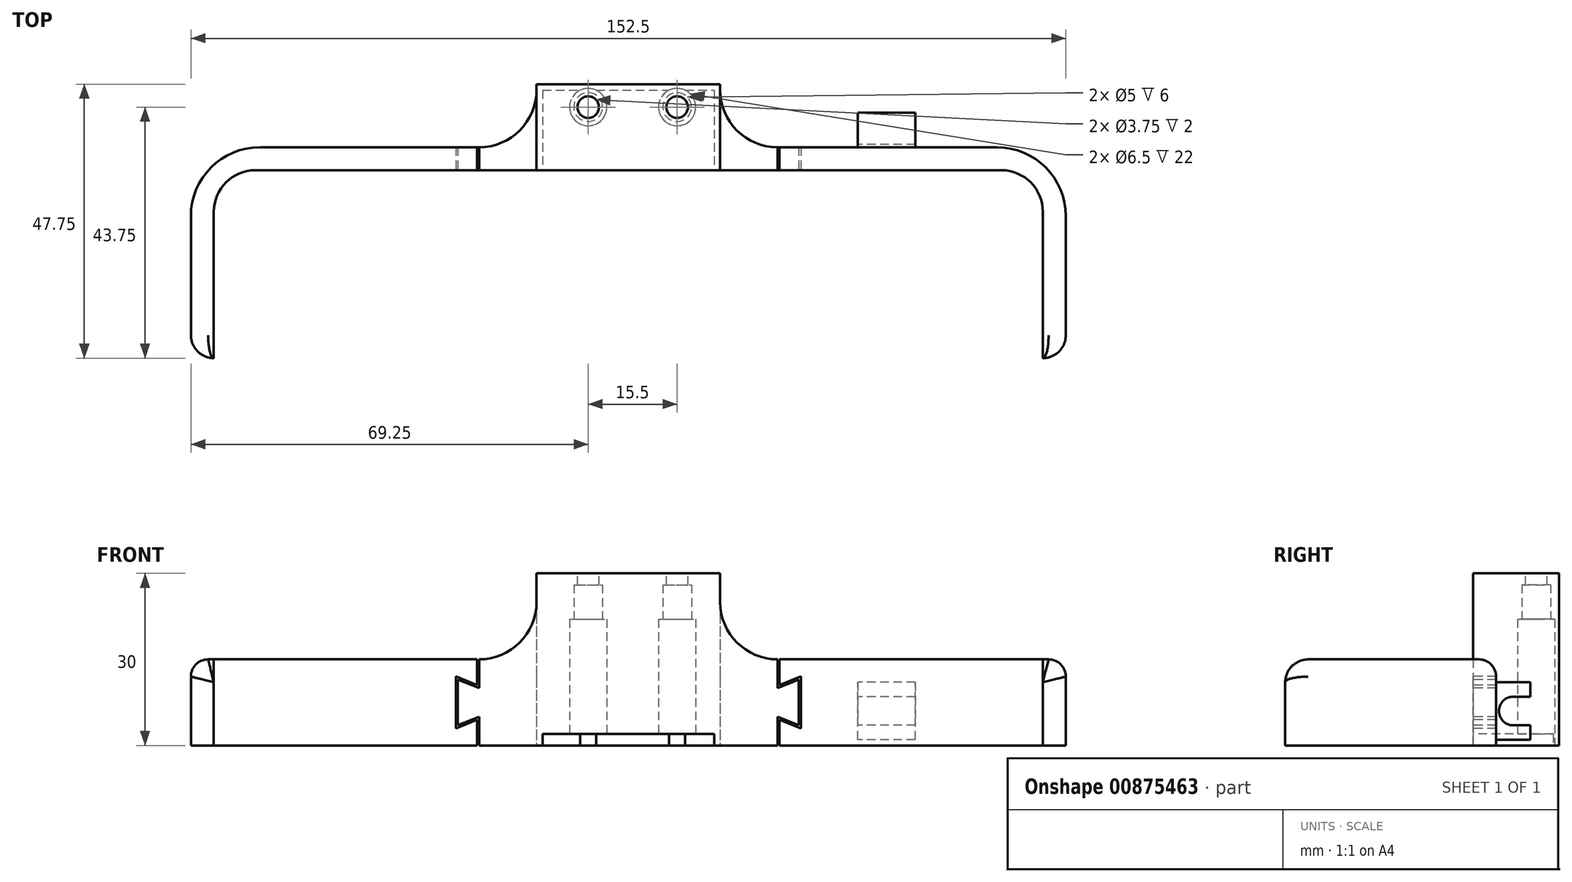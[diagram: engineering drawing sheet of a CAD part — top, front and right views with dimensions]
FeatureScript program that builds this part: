
annotation { "Feature Type Name" : "Feature", "Feature Type Description" : "" }
export const myFeature = defineFeature(function(context is Context, id is Id, definition is map)
    precondition{}
    {
        {
            var Q0;
            Q0=qCreatedBy(makeId("Top.planeOp"),FACE);
            var sketch = newSketch(context, id + "F0", { "sketchPlane" : qUnion([Q0])});
            skLineSegment(sketch, "E0.bottom", {"start": v(-65, 47.5) * mm, "end": v(65, 47.5) * mm, "construction": true});
            skLineSegment(sketch, "E0.top", {"start": v(-65, -47.5) * mm, "end": v(65, -47.5) * mm, "construction": true});
            skLineSegment(sketch, "E0.left", {"start": v(-72, 40.5) * mm, "end": v(-72, -40.5) * mm, "construction": true});
            skLineSegment(sketch, "E0.right", {"start": v(72, 40.5) * mm, "end": v(72, -40.5) * mm, "construction": true});
            skPoint(sketch, "E0.middle", {"position": v(0, 0) * mm});
            skPoint(sketch, "E1.visualSharp", {"position": v(-72, 47.5) * mm});
            skArc(sketch, "E1.filletArc", {"start": v(-65, 47.5) * mm, "mid": v(-69.95, 45.45) * mm, "end": v(-72, 40.5) * mm, "construction": true});
            skPoint(sketch, "E2.visualSharp", {"position": v(72, 47.5) * mm});
            skArc(sketch, "E2.filletArc", {"start": v(72, 40.5) * mm, "mid": v(69.95, 45.45) * mm, "end": v(65, 47.5) * mm, "construction": true});
            skPoint(sketch, "E3.visualSharp", {"position": v(72, -47.5) * mm});
            skArc(sketch, "E3.filletArc", {"start": v(65, -47.5) * mm, "mid": v(69.95, -45.45) * mm, "end": v(72, -40.5) * mm, "construction": true});
            skPoint(sketch, "E4.visualSharp", {"position": v(-72, -47.5) * mm});
            skArc(sketch, "E4.filletArc", {"start": v(-72, -40.5) * mm, "mid": v(-69.95, -45.45) * mm, "end": v(-65, -47.5) * mm, "construction": true});
            skPoint(sketch, "E5.firstSnap0", {"position": v(0, 47.5) * mm});
            skLineSegment(sketch, "E5.bottom", {"start": v(0, 47.75) * mm, "end": v(-72.25, 47.75) * mm});
            skLineSegment(sketch, "E5.top", {"start": v(0, 51.75) * mm, "end": v(-76.25, 51.75) * mm});
            skLineSegment(sketch, "E5.left", {"start": v(0, 47.75) * mm, "end": v(0, 51.75) * mm});
            skLineSegment(sketch, "E5.right", {"start": v(-76.25, 47.75) * mm, "end": v(-76.25, 51.75) * mm, "construction": true});
            skLineSegment(sketch, "E6.bottom", {"start": v(-76.25, 51.75) * mm, "end": v(-72.25, 51.75) * mm, "construction": true});
            skLineSegment(sketch, "E6.top", {"start": v(-76.25, -47.75) * mm, "end": v(-72.25, -47.75) * mm});
            skLineSegment(sketch, "E6.left", {"start": v(-76.25, 51.75) * mm, "end": v(-76.25, -47.75) * mm});
            skLineSegment(sketch, "E6.right", {"start": v(-72.25, 47.75) * mm, "end": v(-72.25, -47.75) * mm});
            skLineSegment(sketch, "E7", {"start": v(0, 47.5) * mm, "end": v(0, 47.75) * mm, "construction": true});
            skLineSegment(sketch, "E8", {"start": v(-72, 0) * mm, "end": v(-72.25, 0) * mm, "construction": true});
            skPoint(sketch, "E9", {"position": v(-72.25, 47.75) * mm});
            skLineSegment(sketch, "E10.bottom", {"start": v(-76.25, -47.75) * mm, "end": v(-50.25, -47.75) * mm});
            skLineSegment(sketch, "E10.top", {"start": v(-76.25, -51.75) * mm, "end": v(-50.25, -51.75) * mm});
            skLineSegment(sketch, "E10.left", {"start": v(-76.25, -47.75) * mm, "end": v(-76.25, -51.75) * mm});
            skLineSegment(sketch, "E10.right", {"start": v(-50.25, -47.75) * mm, "end": v(-50.25, -51.75) * mm});
            skLineSegment(sketch, "E11", {"start": v(-50.25, -47.75) * mm, "end": v(-50.25, -47.5) * mm, "construction": true});
            skLineSegment(sketch, "E12", {"start": v(0, 47.5) * mm, "end": v(0, -47.5) * mm, "construction": true});
            skArc(sketch, "E13", {"start": v(-65, 47.75) * mm, "mid": v(-70.13, 45.63) * mm, "end": v(-72.25, 40.5) * mm});
            skArc(sketch, "E14", {"start": v(-72.25, -40.5) * mm, "mid": v(-70.13, -45.63) * mm, "end": v(-65, -47.75) * mm});
            skLineSegment(sketch, "E15", {"start": v(-72.25, 47.75) * mm, "end": v(-76.25, 47.75) * mm, "construction": true});
            skLineSegment(sketch, "E16", {"start": v(-72.25, 47.75) * mm, "end": v(-72.25, 51.75) * mm, "construction": true});
            skSolve(sketch);
        }
        {
            var Q0;
            Q0 = qSketchRegion(id + "F0", true);
            extrude(context, id + "F1", {"entities" : qUnion([Q0]), "depth" : 15 * mm, "offsetDistance" : 25 * mm});
        }
        {
            var Q0;
            Q0=makeQuery(id+"F1.opExtrude","SWEPT_BODY",BODY,{"disambiguationData":[OSD([sQuery(id+"F0.wireOp",EDGE,"E5.bottom"),sQuery(id+"F0.wireOp",EDGE,"E5.top"),sQuery(id+"F0.wireOp",EDGE,"E5.left"),sQuery(id+"F0.wireOp",EDGE,"E5.right"),sQuery(id+"F0.wireOp",EDGE,"E6.left"),sQuery(id+"F0.wireOp",EDGE,"E6.right"),sQuery(id+"F0.wireOp",EDGE,"E10.bottom"),sQuery(id+"F0.wireOp",EDGE,"E10.top"),sQuery(id+"F0.wireOp",EDGE,"E10.left"),sQuery(id+"F0.wireOp",EDGE,"E10.right")])]});
            var Q1;
            Q1=makeQuery(id+"F1.opExtrude","SWEPT_FACE",FACE,{"disambiguationData":[OSD([sQuery(id+"F0.wireOp",EDGE,"E5.left")])]});
            mirror(context, id + "F2", {"operationType" : NewBodyOperationType.ADD, "entities" : qUnion([Q0]), "mirrorPlane" : qUnion([Q1])});
        }
        {
            var Q0;
            Q0=makeQuery(id+"F2.opPattern","COPY",FACE,{"derivedFrom":makeQuery(id+"F1.opExtrude","SWEPT_FACE",FACE,{"disambiguationData":[OSD([sQuery(id+"F0.wireOp",EDGE,"E6.left"),sQuery(id+"F0.wireOp",EDGE,"E10.left")])]}),"instanceName":"1"});
            var sketch = newSketch(context, id + "F3", { "sketchPlane" : qUnion([Q0])});
            skLineSegment(sketch, "E17.bottom", {"start": v(-11.5, 4.5) * mm, "end": v(11.5, 4.5) * mm});
            skLineSegment(sketch, "E17.top", {"start": v(-11.5, 15) * mm, "end": v(11.5, 15) * mm});
            skLineSegment(sketch, "E17.left", {"start": v(-11.5, 4.5) * mm, "end": v(-11.5, 15) * mm});
            skLineSegment(sketch, "E17.right", {"start": v(11.5, 4.5) * mm, "end": v(11.5, 15) * mm});
            skPoint(sketch, "E18", {"position": v(0, 4.5) * mm});
            skSolve(sketch);
        }
        {
            var Q0;
            Q0 = qSketchRegion(id + "F3", true);
            extrude(context, id + "F4", {"entities" : qUnion([Q0]), "operationType" : NewBodyOperationType.REMOVE, "endBound" : BoundingType.THROUGH_ALL, "oppositeDirection" : true, "depth" : 25 * mm, "offsetDistance" : 25 * mm});
        }
        {
            var Q0;
            Q0=makeQuery(id+"F2.opPattern","COPY",EDGE,{"derivedFrom":makeQuery(id+"F1.opExtrude","SWEPT_EDGE",EDGE,{"disambiguationData":[OSD([sQuery(id+"F0.wireOp",EDGE,"E10.top"),sQuery(id+"F0.wireOp",EDGE,"E10.left")])]}),"instanceName":"1"});
            var Q1;
            Q1=makeQuery(id+"F2.opPattern","COPY",EDGE,{"derivedFrom":makeQuery(id+"F1.opExtrude","SWEPT_EDGE",EDGE,{"disambiguationData":[OSD([sQuery(id+"F0.wireOp",EDGE,"E5.top"),sQuery(id+"F0.wireOp",EDGE,"E6.left")])]}),"instanceName":"1"});
            var Q2;
            Q2=makeQuery(id+"F1.opExtrude","SWEPT_EDGE",EDGE,{"disambiguationData":[OSD([sQuery(id+"F0.wireOp",EDGE,"E10.top"),sQuery(id+"F0.wireOp",EDGE,"E10.left")])]});
            var Q3;
            Q3=makeQuery(id+"F1.opExtrude","SWEPT_EDGE",EDGE,{"disambiguationData":[OSD([sQuery(id+"F0.wireOp",EDGE,"E5.top"),sQuery(id+"F0.wireOp",EDGE,"E6.left")])]});
            fillet(context, id + "F5", {"entities" : qUnion([Q0, Q1, Q2, Q3]), "tangentPropagation" : true, "radius" : 12 * mm, "defaultsChanged" : true, "vertexSettings" : [], "allowEdgeOverflow" : false});
        }
        {
            var Q0;
            Q0=qCreatedBy(makeId("Top.planeOp"),FACE);
            var sketch = newSketch(context, id + "F6", { "sketchPlane" : qUnion([Q0])});
            skLineSegment(sketch, "E19.bottom", {"start": v(-16, 47.75) * mm, "end": v(16, 47.75) * mm});
            skLineSegment(sketch, "E19.top", {"start": v(-16, 62.75) * mm, "end": v(16, 62.75) * mm});
            skLineSegment(sketch, "E19.left", {"start": v(-16, 47.75) * mm, "end": v(-16, 62.75) * mm});
            skLineSegment(sketch, "E19.right", {"start": v(16, 47.75) * mm, "end": v(16, 62.75) * mm});
            skPoint(sketch, "E20", {"position": v(0, 62.75) * mm});
            skSolve(sketch);
        }
        {
            var Q0;
            Q0 = qSketchRegion(id + "F6", true);
            extrude(context, id + "F7", {"entities" : qUnion([Q0]), "operationType" : NewBodyOperationType.ADD, "depth" : 30 * mm, "offsetDistance" : 25 * mm});
        }
        {
            var Q0;
            Q0=makeQuery(id+"F2.opPattern","COPY",EDGE,{"derivedFrom":makeQuery(id+"F1.opExtrude","CAP_EDGE",EDGE,{"disambiguationData":[OSD([sQuery(id+"F0.wireOp",EDGE,"E6.left"),sQuery(id+"F0.wireOp",EDGE,"E10.left")])],"isStart":false}),"instanceName":"1"});
            var Q1;
            Q1=makeQuery(id+"F1.opExtrude","CAP_EDGE",EDGE,{"disambiguationData":[OSD([sQuery(id+"F0.wireOp",EDGE,"E6.left"),sQuery(id+"F0.wireOp",EDGE,"E10.left")])],"isStart":false});
            var Q2;
            Q2=makeQuery(id+"F1.opExtrude","SWEPT_EDGE",EDGE,{"disambiguationData":[OSD([sQuery(id+"F0.wireOp",EDGE,"E10.top"),sQuery(id+"F0.wireOp",EDGE,"E10.right")])]});
            var Q3;
            Q3=makeQuery(id+"F2.opPattern","COPY",EDGE,{"derivedFrom":makeQuery(id+"F1.opExtrude","SWEPT_EDGE",EDGE,{"disambiguationData":[OSD([sQuery(id+"F0.wireOp",EDGE,"E10.top"),sQuery(id+"F0.wireOp",EDGE,"E10.right")])]}),"instanceName":"1"});
            var Q4;
            Q4=makeQuery(id+"F4.boolean.opBoolean","COPY",EDGE,{"derivedFrom":makeQuery(id+"F4.opExtrude","CAP_EDGE",EDGE,{"disambiguationData":[OSD([sQuery(id+"F3.wireOp",EDGE,"E17.right")])],"isStart":true})});
            var Q5;
            Q5=makeQuery(id+"F4.boolean.opBoolean","COPY",EDGE,{"derivedFrom":makeQuery(id+"F4.opExtrude","CAP_EDGE",EDGE,{"disambiguationData":[OSD([sQuery(id+"F3.wireOp",EDGE,"E17.left")])],"isStart":true})});
            var Q6;
            Q6=makeQuery(id+"F4.boolean.opBoolean","INTERSECT",EDGE,{"derivedFrom":[makeQuery(id+"F1.opExtrude","SWEPT_FACE",FACE,{"disambiguationData":[OSD([sQuery(id+"F0.wireOp",EDGE,"E6.left"),sQuery(id+"F0.wireOp",EDGE,"E10.left")])]}),makeQuery(id+"F4.opExtrude","SWEPT_FACE",FACE,{"disambiguationData":[OSD([sQuery(id+"F3.wireOp",EDGE,"E17.right")])]})]});
            var Q7;
            Q7=makeQuery(id+"F4.boolean.opBoolean","INTERSECT",EDGE,{"derivedFrom":[makeQuery(id+"F1.opExtrude","SWEPT_FACE",FACE,{"disambiguationData":[OSD([sQuery(id+"F0.wireOp",EDGE,"E6.left"),sQuery(id+"F0.wireOp",EDGE,"E10.left")])]}),makeQuery(id+"F4.opExtrude","SWEPT_FACE",FACE,{"disambiguationData":[OSD([sQuery(id+"F3.wireOp",EDGE,"E17.left")])]})]});
            fillet(context, id + "F8", {"entities" : qUnion([Q0, Q1, Q2, Q3, Q4, Q5, Q6, Q7]), "tangentPropagation" : true, "radius" : 3 * mm, "defaultsChanged" : false, "vertexSettings" : [], "allowEdgeOverflow" : false});
        }
        {
            var Q0;
            {var subQ0=makeQuery(id+"F1.opExtrude","SWEPT_FACE",FACE,{"disambiguationData":[OSD([sQuery(id+"F0.wireOp",EDGE,"E5.top")])]});Q0=makeQuery(id+"F7.boolean.opBoolean","INTERSECT",EDGE,{"derivedFrom":[makeQuery(id+"F2.boolean.opBoolean","MERGE",FACE,{"derivedFrom":[subQ0,makeQuery(id+"F2.opPattern","COPY",FACE,{"derivedFrom":subQ0,"instanceName":"1"})]}),makeQuery(id+"F7.opExtrude","SWEPT_FACE",FACE,{"disambiguationData":[OSD([sQuery(id+"F6.wireOp",EDGE,"E19.left")])]})]});}
            var Q1;
            {var subQ0=makeQuery(id+"F1.opExtrude","SWEPT_FACE",FACE,{"disambiguationData":[OSD([sQuery(id+"F0.wireOp",EDGE,"E5.top")])]});Q1=makeQuery(id+"F7.boolean.opBoolean","INTERSECT",EDGE,{"derivedFrom":[makeQuery(id+"F2.boolean.opBoolean","MERGE",FACE,{"derivedFrom":[subQ0,makeQuery(id+"F2.opPattern","COPY",FACE,{"derivedFrom":subQ0,"instanceName":"1"})]}),makeQuery(id+"F7.opExtrude","SWEPT_FACE",FACE,{"disambiguationData":[OSD([sQuery(id+"F6.wireOp",EDGE,"E19.right")])]})]});}
            fillet(context, id + "F9", {"entities" : qUnion([Q0, Q1]), "tangentPropagation" : true, "radius" : 10 * mm, "defaultsChanged" : true, "vertexSettings" : [], "allowEdgeOverflow" : false});
        }
        {
            var Q0;
            Q0=makeQuery(id+"F7.opExtrude","CAP_FACE",FACE,{"disambiguationData":[OSD([sQuery(id+"F6.wireOp",EDGE,"E19.bottom"),sQuery(id+"F6.wireOp",EDGE,"E19.top"),sQuery(id+"F6.wireOp",EDGE,"E19.left"),sQuery(id+"F6.wireOp",EDGE,"E19.right")])],"isStart":false});
            var sketch = newSketch(context, id + "F10", { "sketchPlane" : qUnion([Q0])});
            skLineSegment(sketch, "E21", {"start": v(-16, 58.75) * mm, "end": v(16, 58.75) * mm, "construction": true});
            skCircle(sketch, "E22", {"center": v(8.5, 58.75) * mm, "radius": 1.88 * mm});
            skCircle(sketch, "E23", {"center": v(-7, 58.75) * mm, "radius": 1.88 * mm});
            skSolve(sketch);
        }
        {
            var Q0;
            Q0 = qSketchRegion(id + "F10", true);
            extrude(context, id + "F11", {"entities" : qUnion([Q0]), "operationType" : NewBodyOperationType.REMOVE, "endBound" : BoundingType.THROUGH_ALL, "oppositeDirection" : true, "depth" : 25 * mm, "offsetDistance" : 25 * mm});
        }
        {
            var Q0;
            {var subQ0=makeQuery(id+"F1.opExtrude","CAP_FACE",FACE,{"disambiguationData":[OSD([sQuery(id+"F0.wireOp",EDGE,"E5.bottom"),sQuery(id+"F0.wireOp",EDGE,"E5.top"),sQuery(id+"F0.wireOp",EDGE,"E5.left"),sQuery(id+"F0.wireOp",EDGE,"E6.left"),sQuery(id+"F0.wireOp",EDGE,"E6.right"),sQuery(id+"F0.wireOp",EDGE,"E10.bottom"),sQuery(id+"F0.wireOp",EDGE,"E10.top"),sQuery(id+"F0.wireOp",EDGE,"E10.left"),sQuery(id+"F0.wireOp",EDGE,"E10.right"),sQuery(id+"F0.wireOp",EDGE,"E13"),sQuery(id+"F0.wireOp",EDGE,"E14")])],"isStart":true});Q0=makeQuery(id+"F7.boolean.opBoolean","MERGE",FACE,{"derivedFrom":[makeQuery(id+"F2.boolean.opBoolean","MERGE",FACE,{"derivedFrom":[subQ0,makeQuery(id+"F2.opPattern","COPY",FACE,{"derivedFrom":subQ0,"instanceName":"1"})]}),makeQuery(id+"F7.opExtrude","CAP_FACE",FACE,{"disambiguationData":[OSD([sQuery(id+"F6.wireOp",EDGE,"E19.bottom"),sQuery(id+"F6.wireOp",EDGE,"E19.top"),sQuery(id+"F6.wireOp",EDGE,"E19.left"),sQuery(id+"F6.wireOp",EDGE,"E19.right")])],"isStart":true})]});}
            var sketch = newSketch(context, id + "F12", { "sketchPlane" : qUnion([Q0])});
            skCircle(sketch, "E24", {"center": v(-7, -58.75) * mm, "radius": 2.5 * mm});
            skCircle(sketch, "E25", {"center": v(8.5, -58.75) * mm, "radius": 2.5 * mm});
            skSolve(sketch);
        }
        {
            var Q0;
            Q0 = qSketchRegion(id + "F12", true);
            extrude(context, id + "F13", {"entities" : qUnion([Q0]), "operationType" : NewBodyOperationType.REMOVE, "oppositeDirection" : true, "depth" : 28 * mm, "offsetDistance" : 25 * mm});
        }
        {
            var Q0;
            {var subQ0=makeQuery(id+"F1.opExtrude","CAP_FACE",FACE,{"disambiguationData":[OSD([sQuery(id+"F0.wireOp",EDGE,"E5.bottom"),sQuery(id+"F0.wireOp",EDGE,"E5.top"),sQuery(id+"F0.wireOp",EDGE,"E5.left"),sQuery(id+"F0.wireOp",EDGE,"E6.left"),sQuery(id+"F0.wireOp",EDGE,"E6.right"),sQuery(id+"F0.wireOp",EDGE,"E10.bottom"),sQuery(id+"F0.wireOp",EDGE,"E10.top"),sQuery(id+"F0.wireOp",EDGE,"E10.left"),sQuery(id+"F0.wireOp",EDGE,"E10.right"),sQuery(id+"F0.wireOp",EDGE,"E13"),sQuery(id+"F0.wireOp",EDGE,"E14")])],"isStart":true});Q0=makeQuery(id+"F7.boolean.opBoolean","MERGE",FACE,{"derivedFrom":[makeQuery(id+"F2.boolean.opBoolean","MERGE",FACE,{"derivedFrom":[subQ0,makeQuery(id+"F2.opPattern","COPY",FACE,{"derivedFrom":subQ0,"instanceName":"1"})]}),makeQuery(id+"F7.opExtrude","CAP_FACE",FACE,{"disambiguationData":[OSD([sQuery(id+"F6.wireOp",EDGE,"E19.bottom"),sQuery(id+"F6.wireOp",EDGE,"E19.top"),sQuery(id+"F6.wireOp",EDGE,"E19.left"),sQuery(id+"F6.wireOp",EDGE,"E19.right")])],"isStart":true})]});}
            var sketch = newSketch(context, id + "F14", { "sketchPlane" : qUnion([Q0])});
            skCircle(sketch, "E26", {"center": v(-7, -58.75) * mm, "radius": 3.25 * mm});
            skCircle(sketch, "E27", {"center": v(8.5, -58.75) * mm, "radius": 3.25 * mm});
            skSolve(sketch);
        }
        {
            var Q0;
            Q0 = qSketchRegion(id + "F14", true);
            extrude(context, id + "F15", {"entities" : qUnion([Q0]), "operationType" : NewBodyOperationType.REMOVE, "oppositeDirection" : true, "depth" : (30 - 2 - 6) * mm, "offsetDistance" : 25 * mm});
        }
        {
            var Q0;
            Q0=qCreatedBy(makeId("Front.planeOp"),FACE);
            cPlane(context, id + "F16", {"entities" : qUnion([Q0]), "cplaneType" : CPlaneType.OFFSET, "offset" : 15 * mm, "oppositeDirection" : true, "width" : 150 * mm, "height" : 150 * mm});
        }
        {
            var Q0;
            Q0=qCreatedBy(id+"F16.planeOp",FACE);
            var sketch = newSketch(context, id + "F17", { "sketchPlane" : qUnion([Q0])});
            skLineSegment(sketch, "E28.bottom", {"start": v(-79.6, 0) * mm, "end": v(80.99, 0) * mm});
            skLineSegment(sketch, "E28.top", {"start": v(-79.6, 15) * mm, "end": v(80.99, 15) * mm});
            skLineSegment(sketch, "E28.left", {"start": v(-79.6, 0) * mm, "end": v(-79.6, 15) * mm});
            skLineSegment(sketch, "E28.right", {"start": v(80.99, 0) * mm, "end": v(80.99, 15) * mm});
            skSolve(sketch);
        }
        {
            var Q0;
            Q0 = qSketchRegion(id + "F17", true);
            extrude(context, id + "F18", {"entities" : qUnion([Q0]), "operationType" : NewBodyOperationType.REMOVE, "endBound" : BoundingType.THROUGH_ALL, "depth" : 25 * mm, "offsetDistance" : 25 * mm});
        }
        {
            var Q0;
            Q0=makeQuery(id+"F18.boolean.opBoolean","INTERSECT",EDGE,{"derivedFrom":[makeQuery(id+"F1.opExtrude","SWEPT_FACE",FACE,{"disambiguationData":[OSD([sQuery(id+"F0.wireOp",EDGE,"E6.left"),sQuery(id+"F0.wireOp",EDGE,"E10.left")])]}),makeQuery(id+"F18.opExtrude","CAP_FACE",FACE,{"disambiguationData":[OSD([sQuery(id+"F17.wireOp",EDGE,"E28.bottom"),sQuery(id+"F17.wireOp",EDGE,"E28.top"),sQuery(id+"F17.wireOp",EDGE,"E28.left"),sQuery(id+"F17.wireOp",EDGE,"E28.right")])],"isStart":true})]});
            var Q1;
            Q1=makeQuery(id+"F18.boolean.opBoolean","INTERSECT",EDGE,{"derivedFrom":[makeQuery(id+"F2.opPattern","COPY",FACE,{"derivedFrom":makeQuery(id+"F1.opExtrude","SWEPT_FACE",FACE,{"disambiguationData":[OSD([sQuery(id+"F0.wireOp",EDGE,"E6.left"),sQuery(id+"F0.wireOp",EDGE,"E10.left")])]}),"instanceName":"1"}),makeQuery(id+"F18.opExtrude","CAP_FACE",FACE,{"disambiguationData":[OSD([sQuery(id+"F17.wireOp",EDGE,"E28.bottom"),sQuery(id+"F17.wireOp",EDGE,"E28.top"),sQuery(id+"F17.wireOp",EDGE,"E28.left"),sQuery(id+"F17.wireOp",EDGE,"E28.right")])],"isStart":true})]});
            fillet(context, id + "F19", {"entities" : qUnion([Q0, Q1]), "tangentPropagation" : true, "radius" : 4 * mm, "defaultsChanged" : true, "vertexSettings" : [], "allowEdgeOverflow" : false});
        }
        {
            var Q0;
            {var subQ0=makeQuery(id+"F1.opExtrude","SWEPT_FACE",FACE,{"disambiguationData":[OSD([sQuery(id+"F0.wireOp",EDGE,"E5.bottom")])]});Q0=makeQuery(id+"F7.boolean.opBoolean","MERGE",FACE,{"derivedFrom":[makeQuery(id+"F2.boolean.opBoolean","MERGE",FACE,{"derivedFrom":[subQ0,makeQuery(id+"F2.opPattern","COPY",FACE,{"derivedFrom":subQ0,"instanceName":"1"})]}),makeQuery(id+"F7.opExtrude","SWEPT_FACE",FACE,{"disambiguationData":[OSD([sQuery(id+"F6.wireOp",EDGE,"E19.bottom")])]})]});}
            var sketch = newSketch(context, id + "F20", { "sketchPlane" : qUnion([Q0])});
            skLineSegment(sketch, "E29", {"start": v(-65, 7.5) * mm, "end": v(65, 7.5) * mm, "construction": true});
            skLineSegment(sketch, "E30", {"start": v(-26, 15) * mm, "end": v(-26, 10) * mm});
            skLineSegment(sketch, "E31", {"start": v(-26, 10) * mm, "end": v(-29.7, 11.5) * mm});
            skLineSegment(sketch, "E32", {"start": v(-29.7, 11.5) * mm, "end": v(-29.7, 7.5) * mm});
            skLineSegment(sketch, "E33", {"start": v(-26, 15) * mm, "end": v(-26, 7.5) * mm, "construction": true});
            skLineSegment(sketch, "E34", {"start": v(-26, 15) * mm, "end": v(-26.35, 15) * mm});
            skLineSegment(sketch, "E35", {"start": v(-26.35, 15) * mm, "end": v(-26.35, 10.52) * mm});
            skLineSegment(sketch, "E36", {"start": v(-26.35, 10.52) * mm, "end": v(-30.06, 12.02) * mm});
            skLineSegment(sketch, "E37", {"start": v(-30.06, 12.02) * mm, "end": v(-30.06, 7.5) * mm});
            skLineSegment(sketch, "E38", {"start": v(-26.35, 12.76) * mm, "end": v(-26, 12.76) * mm, "construction": true});
            skLineSegment(sketch, "E39", {"start": v(-29.7, 9.5) * mm, "end": v(-30.06, 9.5) * mm, "construction": true});
            skLineSegment(sketch, "E40", {"start": v(-28.2, 11.27) * mm, "end": v(-28.34, 10.94) * mm, "construction": true});
            skLineSegment(sketch, "E41", {"start": v(-30.06, 7.5) * mm, "end": v(-29.7, 7.5) * mm});
            skLineSegment(sketch, "E42.MirrorCS", {"start": v(-29.7, 3.5) * mm, "end": v(-29.7, 7.5) * mm});
            skLineSegment(sketch, "E43.MirrorCS", {"start": v(-26, 5) * mm, "end": v(-29.7, 3.5) * mm});
            skLineSegment(sketch, "E44.MirrorCS", {"start": v(-26, 0) * mm, "end": v(-26, 7.5) * mm, "construction": true});
            skLineSegment(sketch, "E45.MirrorCS", {"start": v(-26.35, 0) * mm, "end": v(-26.35, 4.48) * mm});
            skLineSegment(sketch, "E46.MirrorCS", {"start": v(-26, 0) * mm, "end": v(-26.35, 0) * mm});
            skLineSegment(sketch, "E47.MirrorCS", {"start": v(-26.35, 4.48) * mm, "end": v(-30.06, 2.98) * mm});
            skLineSegment(sketch, "E48.MirrorCS", {"start": v(-30.06, 2.98) * mm, "end": v(-30.06, 7.5) * mm});
            skLineSegment(sketch, "E49", {"start": v(-26, 5) * mm, "end": v(-26, 0) * mm});
            skLineSegment(sketch, "E50", {"start": v(0, 0) * mm, "end": v(0, 30) * mm, "construction": true});
            skLineSegment(sketch, "E51.MirrorCS", {"start": v(26, 5) * mm, "end": v(26, 0) * mm});
            skLineSegment(sketch, "E52.MirrorCS", {"start": v(26, 0) * mm, "end": v(26, 7.5) * mm, "construction": true});
            skLineSegment(sketch, "E53.MirrorCS", {"start": v(26.35, 0) * mm, "end": v(26.35, 4.48) * mm});
            skLineSegment(sketch, "E54.MirrorCS", {"start": v(26, 5) * mm, "end": v(29.7, 3.5) * mm});
            skLineSegment(sketch, "E55.MirrorCS", {"start": v(26.35, 4.48) * mm, "end": v(30.06, 2.98) * mm});
            skLineSegment(sketch, "E56.MirrorCS", {"start": v(30.06, 2.98) * mm, "end": v(30.06, 7.5) * mm});
            skLineSegment(sketch, "E57.MirrorCS", {"start": v(29.7, 3.5) * mm, "end": v(29.7, 7.5) * mm});
            skLineSegment(sketch, "E58.MirrorCS", {"start": v(28.2, 11.27) * mm, "end": v(28.34, 10.94) * mm, "construction": true});
            skLineSegment(sketch, "E59.MirrorCS", {"start": v(26, 15) * mm, "end": v(26, 10) * mm});
            skLineSegment(sketch, "E60.MirrorCS", {"start": v(29.7, 9.5) * mm, "end": v(30.06, 9.5) * mm, "construction": true});
            skLineSegment(sketch, "E61.MirrorCS", {"start": v(26.35, 12.76) * mm, "end": v(26, 12.76) * mm, "construction": true});
            skLineSegment(sketch, "E62.MirrorCS", {"start": v(29.7, 11.5) * mm, "end": v(29.7, 7.5) * mm});
            skLineSegment(sketch, "E63.MirrorCS", {"start": v(30.06, 12.02) * mm, "end": v(30.06, 7.5) * mm});
            skLineSegment(sketch, "E64.MirrorCS", {"start": v(26.35, 15) * mm, "end": v(26.35, 10.52) * mm});
            skLineSegment(sketch, "E65.MirrorCS", {"start": v(26.35, 10.52) * mm, "end": v(30.06, 12.02) * mm});
            skLineSegment(sketch, "E66.MirrorCS", {"start": v(26, 15) * mm, "end": v(26, 7.5) * mm, "construction": true});
            skLineSegment(sketch, "E67.MirrorCS", {"start": v(26, 10) * mm, "end": v(29.7, 11.5) * mm});
            skLineSegment(sketch, "E68", {"start": v(26, 15) * mm, "end": v(26.35, 15) * mm});
            skLineSegment(sketch, "E69", {"start": v(26, 0) * mm, "end": v(26.35, 0) * mm});
            skSolve(sketch);
        }
        {
            var Q0;
            Q0 = qSketchRegion(id + "F20", true);
            extrude(context, id + "F21", {"entities" : qUnion([Q0]), "operationType" : NewBodyOperationType.REMOVE, "endBound" : BoundingType.THROUGH_ALL, "oppositeDirection" : true, "depth" : 25 * mm, "offsetDistance" : 25 * mm});
        }
        {
            var Q0;
            {var subQ0=sQuery(id+"F6.wireOp",EDGE,"E19.top");var subQ1=sQuery(id+"F0.wireOp",EDGE,"E5.bottom");var subQ3=sQuery(id+"F6.wireOp",EDGE,"E19.bottom");var subQ4=sQuery(id+"F6.wireOp",EDGE,"E19.left");var subQ5=sQuery(id+"F0.wireOp",EDGE,"E5.top");var subQ8=sQuery(id+"F6.wireOp",EDGE,"E19.right");var subQ9=makeQuery(id+"F1.opExtrude","CAP_FACE",FACE,{"disambiguationData":[OSD([subQ1,subQ5,sQuery(id+"F0.wireOp",EDGE,"E5.left"),sQuery(id+"F0.wireOp",EDGE,"E6.left"),sQuery(id+"F0.wireOp",EDGE,"E6.right"),sQuery(id+"F0.wireOp",EDGE,"E10.bottom"),sQuery(id+"F0.wireOp",EDGE,"E10.top"),sQuery(id+"F0.wireOp",EDGE,"E10.left"),sQuery(id+"F0.wireOp",EDGE,"E10.right"),sQuery(id+"F0.wireOp",EDGE,"E13"),sQuery(id+"F0.wireOp",EDGE,"E14")])],"isStart":true});Q0=makeQuery(id+"F21.boolean.opBoolean","SPLIT",FACE,{"disambiguationData":[TD([makeQuery(id+"F7.opExtrude","SWEPT_FACE",FACE,{"disambiguationData":[OSD([subQ0])]})])],"derivedFrom":makeQuery(id+"F7.boolean.opBoolean","MERGE",FACE,{"derivedFrom":[makeQuery(id+"F2.boolean.opBoolean","MERGE",FACE,{"derivedFrom":[subQ9,makeQuery(id+"F2.opPattern","COPY",FACE,{"derivedFrom":subQ9,"instanceName":"1"})]}),makeQuery(id+"F7.opExtrude","CAP_FACE",FACE,{"disambiguationData":[OSD([subQ3,subQ0,subQ4,subQ8])],"isStart":true})]})});}
            var sketch = newSketch(context, id + "F22", { "sketchPlane" : qUnion([Q0])});
            skLineSegment(sketch, "E70.bottom", {"start": v(-14.94, -61.69) * mm, "end": v(14.94, -61.69) * mm});
            skLineSegment(sketch, "E70.top", {"start": v(-14.94, -47.75) * mm, "end": v(14.94, -47.75) * mm});
            skLineSegment(sketch, "E70.left", {"start": v(-14.94, -61.69) * mm, "end": v(-14.94, -47.75) * mm});
            skLineSegment(sketch, "E70.right", {"start": v(14.94, -61.69) * mm, "end": v(14.94, -47.75) * mm});
            skLineSegment(sketch, "E71", {"start": v(-14.94, -61.69) * mm, "end": v(-16, -62.75) * mm, "construction": true});
            skLineSegment(sketch, "E72", {"start": v(14.94, -61.69) * mm, "end": v(16, -62.75) * mm, "construction": true});
            skSolve(sketch);
        }
        {
            var Q0;
            Q0 = qSketchRegion(id + "F22", true);
            extrude(context, id + "F23", {"entities" : qUnion([Q0]), "operationType" : NewBodyOperationType.REMOVE, "oppositeDirection" : true, "depth" : 2 * mm, "offsetDistance" : 25 * mm});
        }
        {
            var Q0;
            Q0=qCreatedBy(makeId("Right.planeOp"),FACE);
            cPlane(context, id + "F24", {"entities" : qUnion([Q0]), "cplaneType" : CPlaneType.OFFSET, "offset" : 40 * mm, "width" : 150 * mm, "height" : 150 * mm});
        }
        {
            var Q0;
            Q0=qCreatedBy(id+"F24.planeOp",FACE);
            var sketch = newSketch(context, id + "F25", { "sketchPlane" : qUnion([Q0])});
            skLineSegment(sketch, "E73.bottom", {"start": v(51.75, 1) * mm, "end": v(57.75, 1) * mm});
            skLineSegment(sketch, "E73.top", {"start": v(51.75, 11) * mm, "end": v(57.75, 11) * mm});
            skLineSegment(sketch, "E73.left", {"start": v(51.75, 1) * mm, "end": v(51.75, 11) * mm});
            skArc(sketch, "E74", {"start": v(54.75, 8.5) * mm, "mid": v(52.25, 6) * mm, "end": v(54.75, 3.5) * mm});
            skLineSegment(sketch, "E75", {"start": v(54.75, 8.5) * mm, "end": v(57.75, 8.5) * mm});
            skLineSegment(sketch, "E76", {"start": v(57.75, 11) * mm, "end": v(57.75, 8.5) * mm});
            skLineSegment(sketch, "E77", {"start": v(57.75, 1) * mm, "end": v(57.75, 3.5) * mm});
            skLineSegment(sketch, "E78", {"start": v(57.75, 3.5) * mm, "end": v(54.75, 3.5) * mm});
            skPoint(sketch, "E79", {"position": v(51.75, 6) * mm});
            skSolve(sketch);
        }
        {
            var Q0;
            Q0 = qSketchRegion(id + "F25", true);
            extrude(context, id + "F26", {"entities" : qUnion([Q0]), "operationType" : NewBodyOperationType.ADD, "depth" : 10 * mm, "offsetDistance" : 25 * mm});
        }
    });
